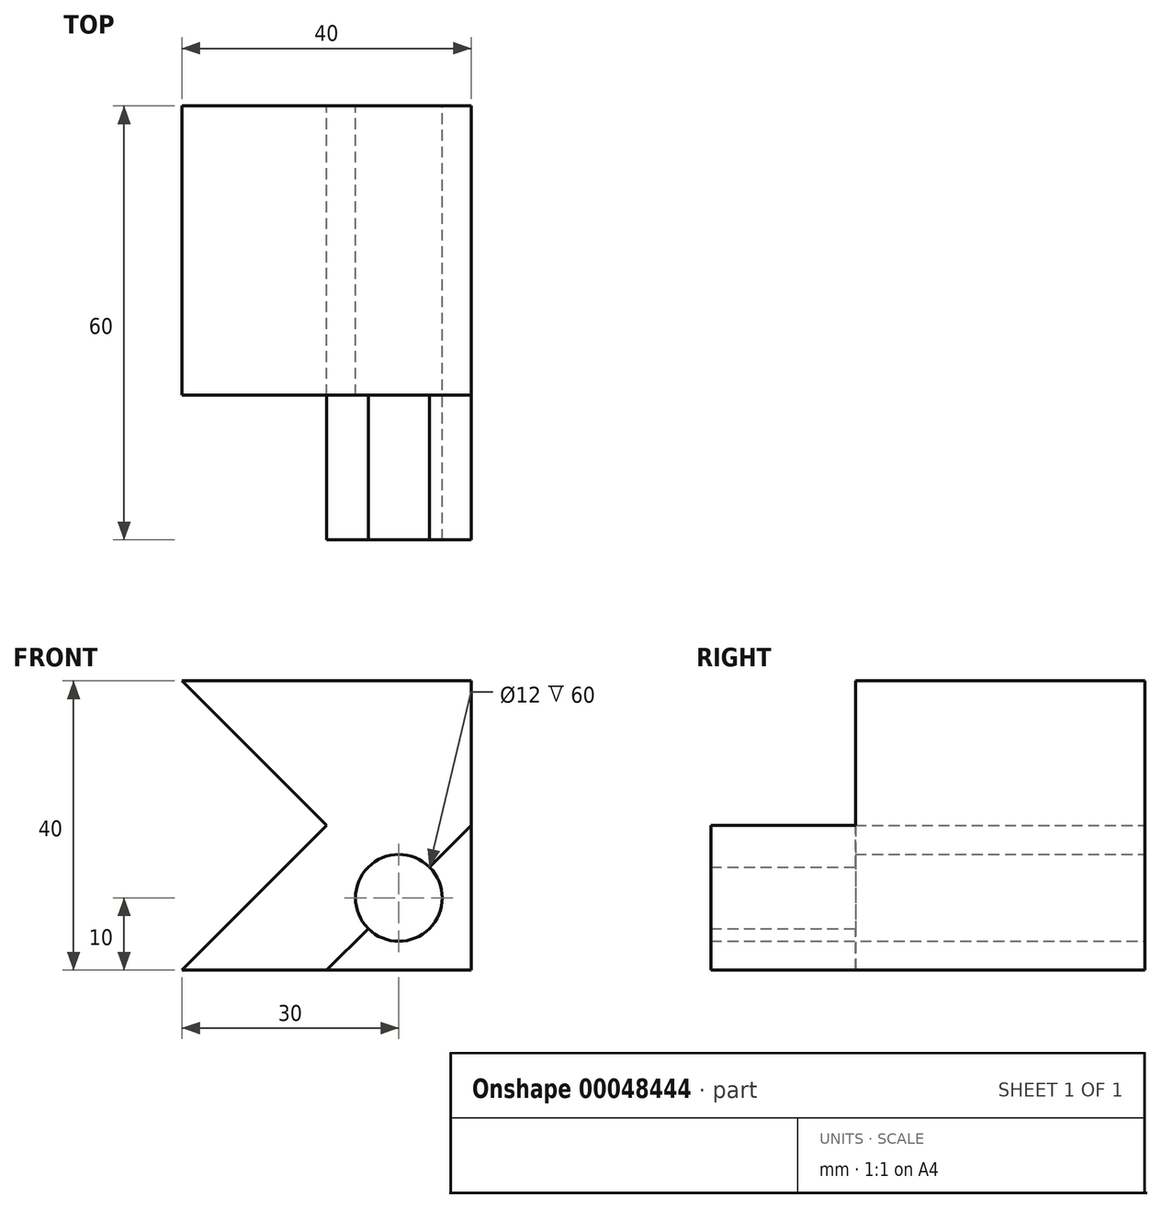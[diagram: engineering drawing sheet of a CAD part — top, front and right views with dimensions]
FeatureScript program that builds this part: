
annotation { "Feature Type Name" : "Feature", "Feature Type Description" : "" }
export const myFeature = defineFeature(function(context is Context, id is Id, definition is map)
    precondition{}
    {
        {
            var Q0;
            Q0=qCreatedBy(makeId("Front.planeOp"),FACE);
            var sketch = newSketch(context, id + "F0", { "sketchPlane" : qUnion([Q0])});
            skLineSegment(sketch, "E0", {"start": v(0, 0) * mm, "end": v(40, 0) * mm});
            skLineSegment(sketch, "E1", {"start": v(40, 0) * mm, "end": v(40, 40) * mm});
            skLineSegment(sketch, "E2", {"start": v(40, 40) * mm, "end": v(0, 40) * mm});
            skLineSegment(sketch, "E3", {"start": v(0, 40) * mm, "end": v(20, 20) * mm});
            skPoint(sketch, "E3.endSnap0", {"position": v(40, 20) * mm});
            skPoint(sketch, "E3.endSnap1", {"position": v(20, 0) * mm});
            skLineSegment(sketch, "E4", {"start": v(20, 20) * mm, "end": v(0, 0) * mm});
            skLineSegment(sketch, "E5", {"start": v(20, 0) * mm, "end": v(40, 20) * mm});
            skCircle(sketch, "E6", {"center": v(30, 10) * mm, "radius": 6 * mm});
            skSolve(sketch);
        }
        {
            var Q0;
            {var subQ4=sQuery(id+"F0.wireOp",EDGE,"E2");Q0=makeQuery(id+"F0.imprint","IMPRINT",FACE,{"disambiguationData":[TD([[makeQuery(id+"F0.imprint","IMPRINT",EDGE,{"derivedFrom":subQ4}),1.0]])]});}
            var Q1;
            {var subQ0=sQuery(id+"F0.wireOp",EDGE,"E6");var subQ1=sQuery(id+"F0.wireOp",EDGE,"E5");var subQ3=makeQuery(id+"F0.imprint","INTERSECT",VERTEX,{"disambiguationData":[OD(0.0)],"derivedFrom":[subQ1,subQ0]});Q1=makeQuery(id+"F0.imprint","IMPRINT",FACE,{"disambiguationData":[TD([[makeQuery(id+"F0.imprint","IMPRINT",EDGE,{"disambiguationData":[TD([[subQ3,-1.0]])],"derivedFrom":subQ1}),1.0]])]});}
            extrude(context, id + "F1", {"entities" : qUnion([Q0, Q1]), "depth" : 40 * mm});
        }
        {
            var Q0;
            {var subQ0=sQuery(id+"F0.wireOp",EDGE,"E5");Q0=makeQuery(id+"F0.imprint","IMPRINT",FACE,{"disambiguationData":[TD([[makeQuery(id+"F0.imprint","IMPRINT",EDGE,{"derivedFrom":subQ0}),-1.0]])]});}
            extrude(context, id + "F2", {"entities" : qUnion([Q0]), "operationType" : NewBodyOperationType.ADD, "depth" : 25 * mm});
        }
        {
            var Q0;
            {var subQ0=sQuery(id+"F0.wireOp",EDGE,"E6");var subQ1=sQuery(id+"F0.wireOp",EDGE,"E5");var subQ3=makeQuery(id+"F0.imprint","INTERSECT",VERTEX,{"disambiguationData":[OD(0.0)],"derivedFrom":[subQ1,subQ0]});Q0=makeQuery(id+"F0.imprint","IMPRINT",FACE,{"disambiguationData":[TD([[makeQuery(id+"F0.imprint","IMPRINT",EDGE,{"disambiguationData":[TD([[subQ3,-1.0]])],"derivedFrom":subQ1}),-1.0]])]});}
            extrude(context, id + "F3", {"entities" : qUnion([Q0]), "operationType" : NewBodyOperationType.ADD, "depth" : 60 * mm});
        }
    });
